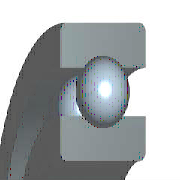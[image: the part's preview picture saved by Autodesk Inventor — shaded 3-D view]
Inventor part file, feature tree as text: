
AUTODESK INVENTOR PART (.ipt)
format: ipt  version: 2025 (Build 290162000, 162)  size: 273,920 bytes
history: native  units: mm (DEFAULTED — no unit token found)
features: other x1, pattern_circular x1
ambient origin geometry x8: Origin, YZ Plane, XZ Plane, XY Plane, X Axis, Y Axis, Z Axis, Center Point
bodies: Solid1 (feature_tree)
feature tree (2):
  other  "轴承体"
  pattern_circular  "IDS_ARRAYBALL[SIMPL:T]"  Angle=90.0deg  [1 undecoded]
note: 1 required parameter value undecoded (feature->parameter linkage not recoverable at this tier; creation-order binding heuristic only, values carry confidence <= 0.55)
